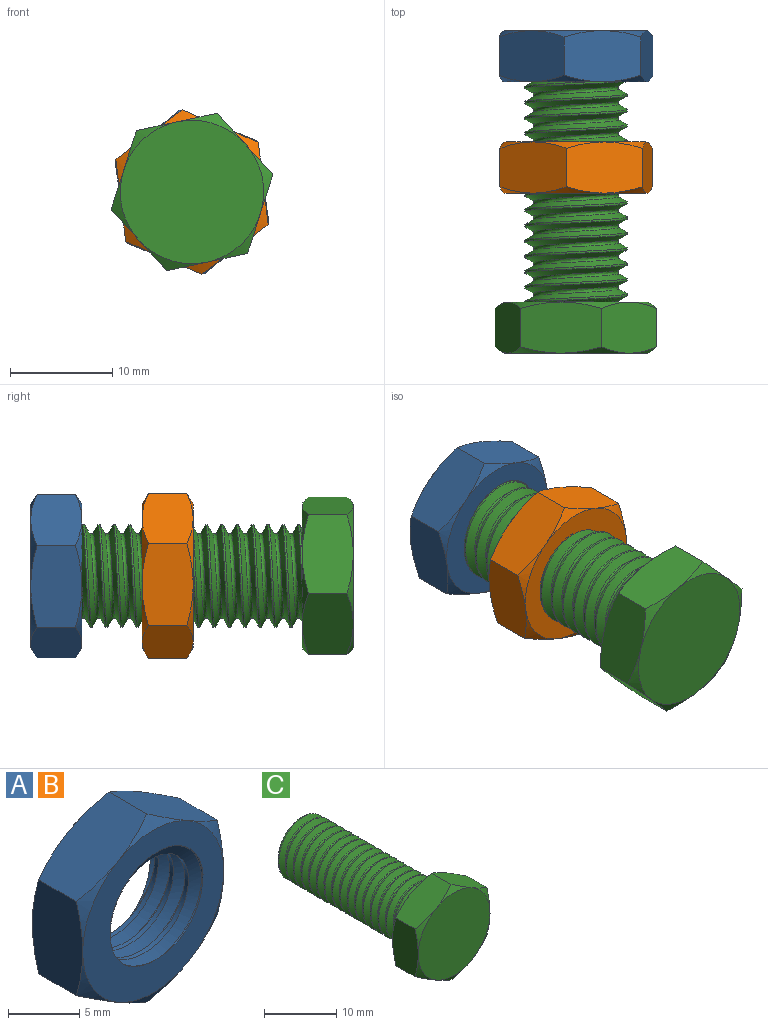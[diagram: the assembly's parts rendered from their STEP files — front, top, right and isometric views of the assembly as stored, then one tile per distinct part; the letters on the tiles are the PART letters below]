
ASSEMBLY  parts=3 mates=2
PART A: 24 faces, bbox 16.8x7x16.8 mm
  f0: plane 14.44x14.44mm, normal (0,-1,0), area 86.9mm2, adj f8,f9,f10,f11,f18,f19,f20,f21
  f1: plane 14.44x14.44mm, normal (0,1,0), area 86.9mm2, adj f8,f9,f10,f11,f12,f13,f14,f15
  f2: plane 7.66x5.67mm, normal (0.5,0,-0.87), area 36.9mm2, adj f3,f7,f13,f17,f19,f23
  f3: plane 8.76x5.67mm, normal (1,0,0), area 36.9mm2, adj f2,f4,f16,f17,f22,f23
  f4: plane 7.66x5.67mm, normal (0.5,0,0.87), area 36.9mm2, adj f3,f5,f15,f16,f21,f22
  f5: plane 7.66x5.67mm, normal (-0.5,0,0.87), area 36.9mm2, adj f4,f6,f14,f15,f20,f21
  f6: plane 8.76x5.67mm, normal (-1,0,0), area 36.9mm2, adj f5,f7,f12,f14,f18,f20
  f7: plane 7.66x5.67mm, normal (-0.5,0,-0.87), area 36.9mm2, adj f2,f6,f12,f13,f18,f19
  f8: bspline ~11.69x10.12mm, area 91.2mm2, adj f0,f1,f10,f11
  f9: bspline ~11.69x10.12mm, area 91.5mm2, adj f0,f1,f10,f11
  f10: bspline ~11.85x10.26mm, area 23.2mm2, adj f0,f1,f8,f9
  f11: cylinder r=4.25mm len=8.5mm, axis (0,1,0), area 32.9mm2, adj f0,f1,f8,f9
  f12: cone r=7mm half-angle=60deg, axis (0,-1,0), area 4.8mm2, adj f1,f6,f7
  f13: cone r=7mm half-angle=60deg, axis (0,-1,0), area 4.8mm2, adj f1,f2,f7
  f14: cone r=7mm half-angle=60deg, axis (0,-1,0), area 4.8mm2, adj f1,f5,f6
  f15: cone r=7mm half-angle=60deg, axis (0,-1,0), area 4.8mm2, adj f1,f4,f5
  f16: cone r=7mm half-angle=60deg, axis (0,-1,0), area 4.8mm2, adj f1,f3,f4
  f17: cone r=7mm half-angle=60deg, axis (0,-1,0), area 4.8mm2, adj f1,f2,f3
  f18: cone r=7mm half-angle=60deg, axis (0,1,0), area 4.8mm2, adj f0,f6,f7
  f19: cone r=7mm half-angle=60deg, axis (0,1,0), area 4.8mm2, adj f0,f2,f7
  f20: cone r=7mm half-angle=60deg, axis (0,1,0), area 4.8mm2, adj f0,f5,f6
  f21: cone r=7mm half-angle=60deg, axis (0,1,0), area 4.8mm2, adj f0,f4,f5
  f22: cone r=7mm half-angle=60deg, axis (0,1,0), area 4.8mm2, adj f0,f3,f4
  f23: cone r=7mm half-angle=60deg, axis (0,1,0), area 4.8mm2, adj f0,f2,f3
PART B: same geometry as A
PART C: 26 faces, bbox 16.8x31.3x16.8 mm
  f0: plane 14.42x14.42mm, normal (0,1,0), area 89.2mm2, adj f2,f3,f4,f5,f7,f8,f9,f10
  f1: plane 8.56x8.42mm, normal (0,1,0), area 55.9mm2, adj f3,f4,f5,f6
  f2: cylinder r=5mm len=24.63mm, axis (0,-1,0), area 41mm2, adj f0,f4,f5,f6
  f3: bspline ~26.13x9.67mm, area 182.1mm2, adj f0,f1,f4,f5
  f4: bspline ~26.22x11.55mm, area 447.9mm2, adj f0,f1,f2,f3,f6
  f5: bspline ~25.72x11.55mm, area 447.8mm2, adj f0,f1,f2,f3,f6
  f6: cone r=5mm half-angle=63.4deg, axis (0,-1,0), area 9.9mm2, adj f1,f2,f4,f5
  f7: cone r=7mm half-angle=60deg, axis (0,-1,0), area 4.8mm2, adj f0,f13,f18
  f8: cone r=7mm half-angle=60deg, axis (0,-1,0), area 4.8mm2, adj f0,f13,f14
  f9: cone r=7mm half-angle=60deg, axis (0,-1,0), area 4.8mm2, adj f0,f14,f15
  f10: cone r=7mm half-angle=60deg, axis (0,-1,0), area 4.8mm2, adj f0,f15,f16
  f11: cone r=7mm half-angle=60deg, axis (0,-1,0), area 4.8mm2, adj f0,f16,f17
  f12: cone r=7mm half-angle=60deg, axis (0,-1,0), area 4.8mm2, adj f0,f17,f18
  f13: plane 7.66x5.67mm, normal (-0.5,0,-0.87), area 36.9mm2, adj f7,f8,f14,f18,f20,f24
  f14: plane 8.76x5.67mm, normal (-1,0,0), area 36.9mm2, adj f8,f9,f13,f15,f23,f24
  f15: plane 7.66x5.67mm, normal (-0.5,0,0.87), area 36.9mm2, adj f9,f10,f14,f16,f22,f23
  f16: plane 7.66x5.67mm, normal (0.5,0,0.87), area 36.9mm2, adj f10,f11,f15,f17,f21,f22
  f17: plane 8.76x5.67mm, normal (1,0,0), area 36.9mm2, adj f11,f12,f16,f18,f19,f21
  f18: plane 7.66x5.67mm, normal (0.5,0,-0.87), area 36.9mm2, adj f7,f12,f13,f17,f19,f20
  f19: cone r=7mm half-angle=60deg, axis (0,1,0), area 4.8mm2, adj f17,f18,f25
  f20: cone r=7mm half-angle=60deg, axis (0,1,0), area 4.8mm2, adj f13,f18,f25
  f21: cone r=7mm half-angle=60deg, axis (0,1,0), area 4.8mm2, adj f16,f17,f25
  f22: cone r=7mm half-angle=60deg, axis (0,1,0), area 4.8mm2, adj f15,f16,f25
  f23: cone r=7mm half-angle=60deg, axis (0,1,0), area 4.8mm2, adj f14,f15,f25
  f24: cone r=7mm half-angle=60deg, axis (0,1,0), area 4.8mm2, adj f13,f14,f25
  f25: plane 14x14mm, normal (0,-1,0), area 153.9mm2, adj f19,f20,f21,f22,f23,f24
PLACE A rot(axis=(0,-1,0),8.3deg) t=(-8.24,28.32,4.17)mm
PLACE B rot(axis=(0.83,0,0.55),180deg) t=(-8.24,22.45,4.17)mm
PLACE C rot(axis=(0,1,0),77.8deg) t=(-8.24,6.82,4.17)mm fixed
MATE cylindrical B.f11 <-> C.f7  axis (0,1,0) through (-8.24,22.45,4.17)mm
MATE cylindrical C.f7 <-> A.f11  axis (0,-1,0) through (-8.24,1.67,4.17)mm
